# Revit family: SLK24
name_source: partatom
category: Lighting Fixtures
units: mm (PartAtom-declared; Revit-internal decimal feet)

## family parameters
Cut with Voids When Loaded = No
Host = Face
Light Source = Yes
OmniClass Number = 23.80.70.11.14.17
OmniClass Title = Direct/Indirect
Part Type = Normal
Room Calculation Point = No
Round Connector Dimension = Use Diameter
Shared = Yes

## types (1)
- SLK24
    Apparent Load = 32 VA
    Assembly Code = D5020200
    Certifications = All luminaires are built to UL and CSA standards
    Color Filter = 16777215
    Connector Description = Lighting Connector
    Default Elevation = 48 "
    Description = The SLK is a retrofit door kit with a contemporary appearance and LED efficacy.
    Dimming Lamp Color Temperature Shift = <None>
    Emit Shape Visible in Rendering = No
    Emit from Rectangle Length = 47 "
    Emit from Rectangle Width = 23 "
    Features = Contemporary style LED retrofit for existing 2x4 prismatic or parabolic troffers with depth 3-1/8Inch or greater • 83 CRI standard or optional 90 CRI for color sensitive applications • Fully integrated hinged door assembly allows for easy installation and rapid troffer conversion • Reduces job site waste by reusing existing fixture housing • High efficiency acrylic center lens features linear prisms for high performance without pixelation • HE lumen packages available • 60,000 hour LEDs at L80 (up to 150,000 hour projected life) for reduced maintenance • Optional architecturally styled integration of daylight and occupancy sensor(s) • Optional SpectraSync™ offers three modes of tunable white solutions and integrates seamlessly into a variety of control systems • NX Distributed Intelligence™ provides options for standalone and networked integrated sensor with wired connectivity for NX system deployments • DLC® (DesignLights Consortium) Qualified, with some Premium Qualified configurations - see www.designlights.org • Five year warranty (Terms and Conditions Apply)
    Housing Material = Paint - Matte White
    Lamp = LED
    Length = 24 "
    Length 02 = 48 "
    Load Classification = Lighting
    Manufacturer = columbia lighting
    Model = SLK24
    Photometric Note = For more Photometric files please refer to the website
    Photometric Web File = SLK24-30HLG-EU.ies
    Power Factor = 1
    Reflector Finish = White Glass
    Tilt Angle = -90.00°
    URL = https://www.currentlighting.com
    Voltage = 120 V
    Warranty = 5 years Warranty
    Wattage Comments = 32W
    Watts = 32 W
    Width = 11.63 "
    Width 1 = 5 "

## geometry (parser evidence)
native form markers: Blend x19, Sweep x3
no freeform markers — native parametric forms only
